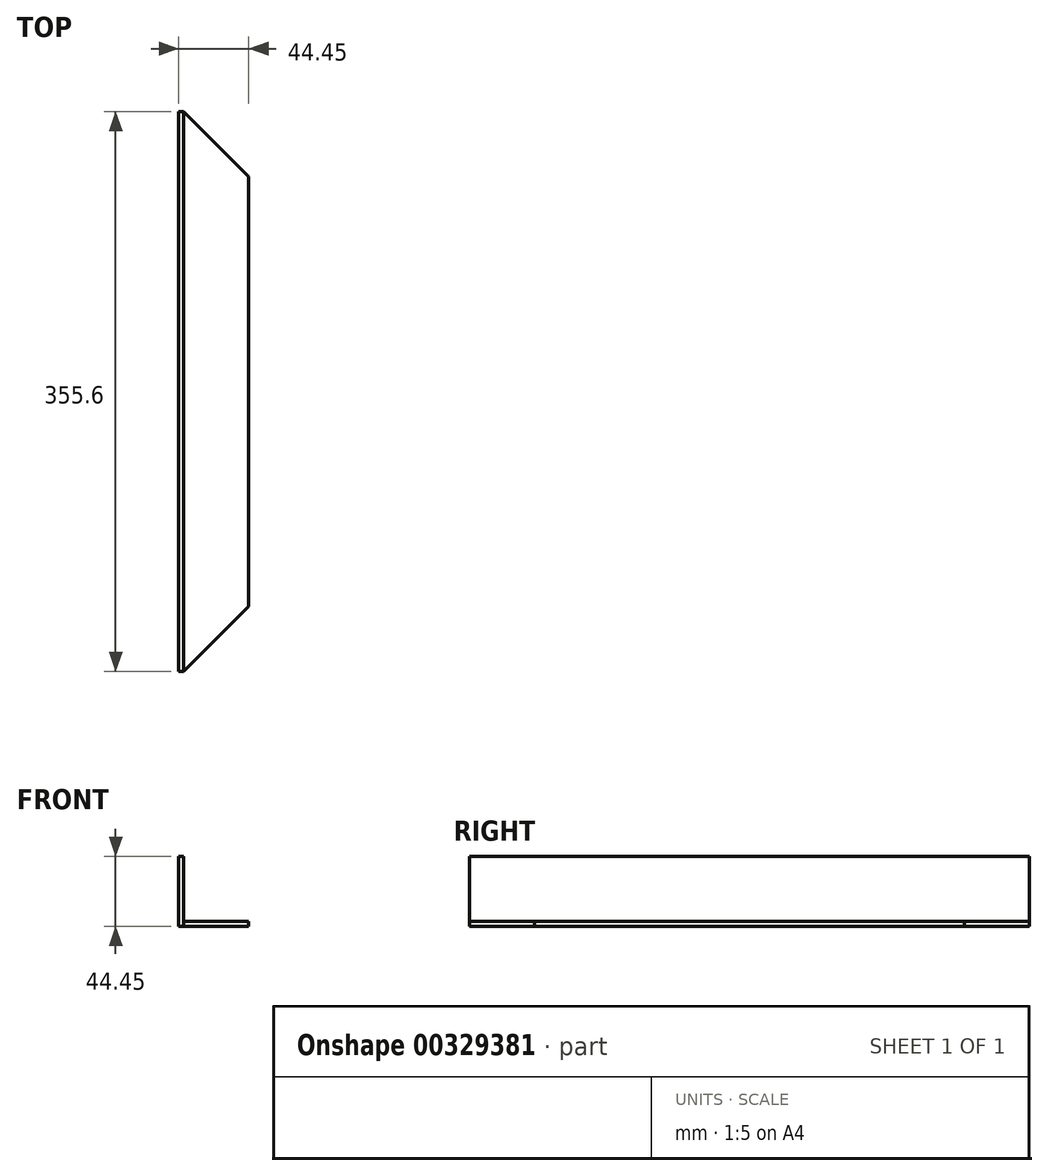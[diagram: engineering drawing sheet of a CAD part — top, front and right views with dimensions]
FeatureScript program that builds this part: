
annotation { "Feature Type Name" : "Feature", "Feature Type Description" : "" }
export const myFeature = defineFeature(function(context is Context, id is Id, definition is map)
    precondition{}
    {
        {
            var Q0;
            Q0=qCreatedBy(makeId("Front.planeOp"),FACE);
            var sketch = newSketch(context, id + "F0", { "sketchPlane" : qUnion([Q0])});
            skLineSegment(sketch, "E0.top", {"start": v(-53.35, -32.52) * mm, "end": v(-8.9, -32.52) * mm});
            skLineSegment(sketch, "E0.left", {"start": v(-53.35, 11.93) * mm, "end": v(-53.35, -32.52) * mm});
            skLineSegment(sketch, "E1.0", {"start": v(-50.17, -29.35) * mm, "end": v(-8.9, -29.35) * mm});
            skLineSegment(sketch, "E1.1", {"start": v(-50.17, 11.93) * mm, "end": v(-50.17, -29.35) * mm});
            skLineSegment(sketch, "E2", {"start": v(-53.35, 11.93) * mm, "end": v(-50.17, 11.93) * mm});
            skLineSegment(sketch, "E3", {"start": v(-8.9, -29.35) * mm, "end": v(-8.9, -32.52) * mm});
            skSolve(sketch);
        }
        {
            var Q0;
            Q0=makeQuery(id+"F0.imprint","IMPRINT",FACE,{"disambiguationData":[TD([[makeQuery(id+"F0.imprint","IMPRINT",EDGE,{"derivedFrom":sQuery(id+"F0.wireOp",EDGE,"E0.top")}),1.0]])]});
            extrude(context, id + "F1", {"entities" : qUnion([Q0]), "depth" : 355.6 * mm});
        }
        {
            var Q0;
            Q0=makeQuery(id+"F1.opExtrude","SWEPT_FACE",FACE,{"disambiguationData":[OSD([sQuery(id+"F0.wireOp",EDGE,"E1.0")])]});
            var sketch = newSketch(context, id + "F2", { "sketchPlane" : qUnion([Q0])});
            skLineSegment(sketch, "E4", {"start": v(-8.9, -41.27) * mm, "end": v(-50.17, 0) * mm});
            skSolve(sketch);
        }
        {
            var Q0;
            {var subQ0=sQuery(id+"F2.wireOp",EDGE,"E4");Q0=makeQuery(id+"F2.imprint","IMPRINT",FACE,{"disambiguationData":[TD([[makeQuery(id+"F2.imprint","IMPRINT",EDGE,{"derivedFrom":subQ0}),-1.0]])]});}
            extrude(context, id + "F3", {"entities" : qUnion([Q0]), "operationType" : NewBodyOperationType.REMOVE, "oppositeDirection" : true, "depth" : 25.4 * mm});
        }
        {
            var Q0;
            Q0=makeQuery(id+"F1.opExtrude","SWEPT_FACE",FACE,{"disambiguationData":[OSD([sQuery(id+"F0.wireOp",EDGE,"E1.0")])]});
            var sketch = newSketch(context, id + "F4", { "sketchPlane" : qUnion([Q0])});
            skLineSegment(sketch, "E5", {"start": v(-8.9, -314.33) * mm, "end": v(-50.17, -355.6) * mm});
            skSolve(sketch);
        }
        {
            var Q0;
            {var subQ0=sQuery(id+"F4.wireOp",EDGE,"E5");Q0=makeQuery(id+"F4.imprint","IMPRINT",FACE,{"disambiguationData":[TD([[makeQuery(id+"F4.imprint","IMPRINT",EDGE,{"derivedFrom":subQ0}),1.0]])]});}
            extrude(context, id + "F5", {"entities" : qUnion([Q0]), "operationType" : NewBodyOperationType.REMOVE, "oppositeDirection" : true, "depth" : 25.4 * mm});
        }
    });
